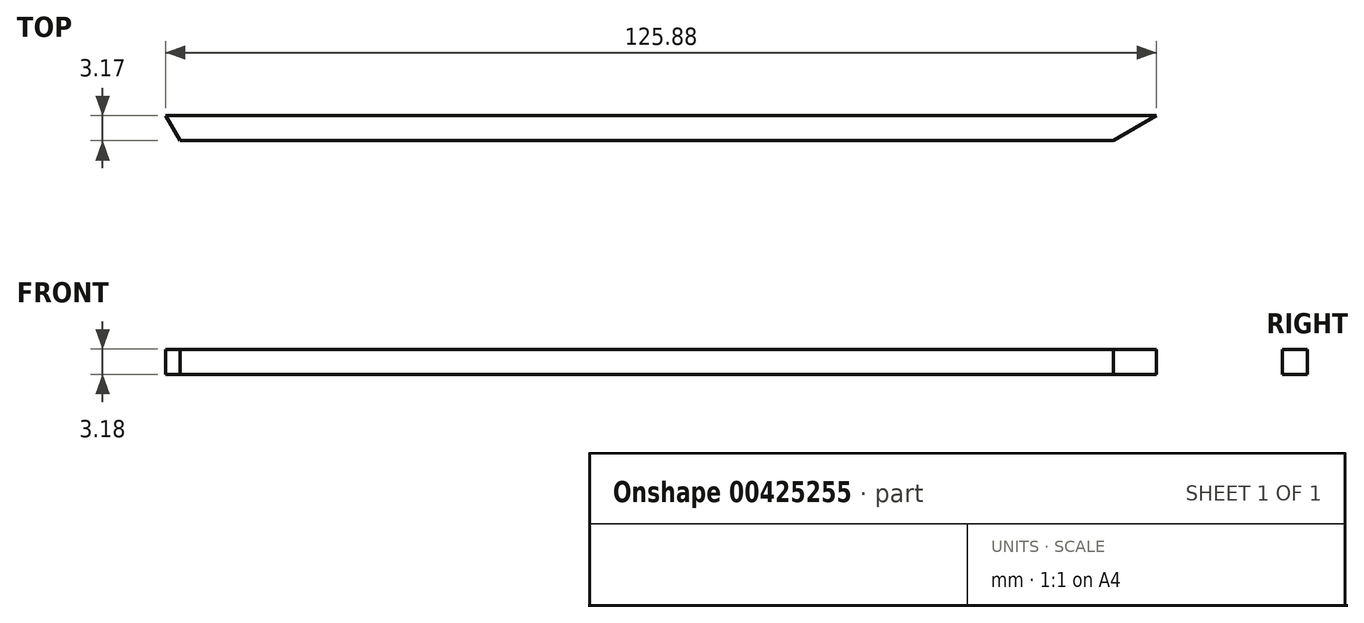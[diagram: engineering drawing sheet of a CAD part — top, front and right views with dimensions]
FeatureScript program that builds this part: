
annotation { "Feature Type Name" : "Feature", "Feature Type Description" : "" }
export const myFeature = defineFeature(function(context is Context, id is Id, definition is map)
    precondition{}
    {
        {
            var Q0;
            Q0=qCreatedBy(makeId("Front.planeOp"),FACE);
            var sketch = newSketch(context, id + "F0", { "sketchPlane" : qUnion([Q0])});
            skLineSegment(sketch, "E0.bottom", {"start": v(-48.92, 35.9) * mm, "end": v(78.08, 35.9) * mm});
            skLineSegment(sketch, "E0.top", {"start": v(-48.92, 32.72) * mm, "end": v(78.08, 32.72) * mm});
            skLineSegment(sketch, "E0.left", {"start": v(-48.92, 35.9) * mm, "end": v(-48.92, 32.72) * mm});
            skLineSegment(sketch, "E0.right", {"start": v(78.08, 35.9) * mm, "end": v(78.08, 32.72) * mm});
            skSolve(sketch);
        }
        {
            var Q0;
            Q0 = qSketchRegion(id + "F0", true);
            extrude(context, id + "F1", {"entities" : qUnion([Q0]), "depth" : 3.17 * mm});
        }
        {
            var Q0;
            Q0=makeQuery(id+"F1.opExtrude","CAP_EDGE",EDGE,{"disambiguationData":[OSD([sQuery(id+"F0.wireOp",EDGE,"E0.left")])],"isStart":false});
            chamfer(context, id + "F2", {"entities" : qUnion([Q0]), "chamferType" : ChamferType.OFFSET_ANGLE, "width" : 2.3 * mm, "oppositeDirection" : false, "angle" : 60 * degree, "tangentPropagation" : true});
        }
        {
            var Q0;
            Q0=makeQuery(id+"F1.opExtrude","CAP_EDGE",EDGE,{"disambiguationData":[OSD([sQuery(id+"F0.wireOp",EDGE,"E0.right")])],"isStart":false});
            chamfer(context, id + "F3", {"entities" : qUnion([Q0]), "chamferType" : ChamferType.OFFSET_ANGLE, "width" : 3.56 * mm, "oppositeDirection" : false, "angle" : 60 * degree, "tangentPropagation" : true});
        }
    });
